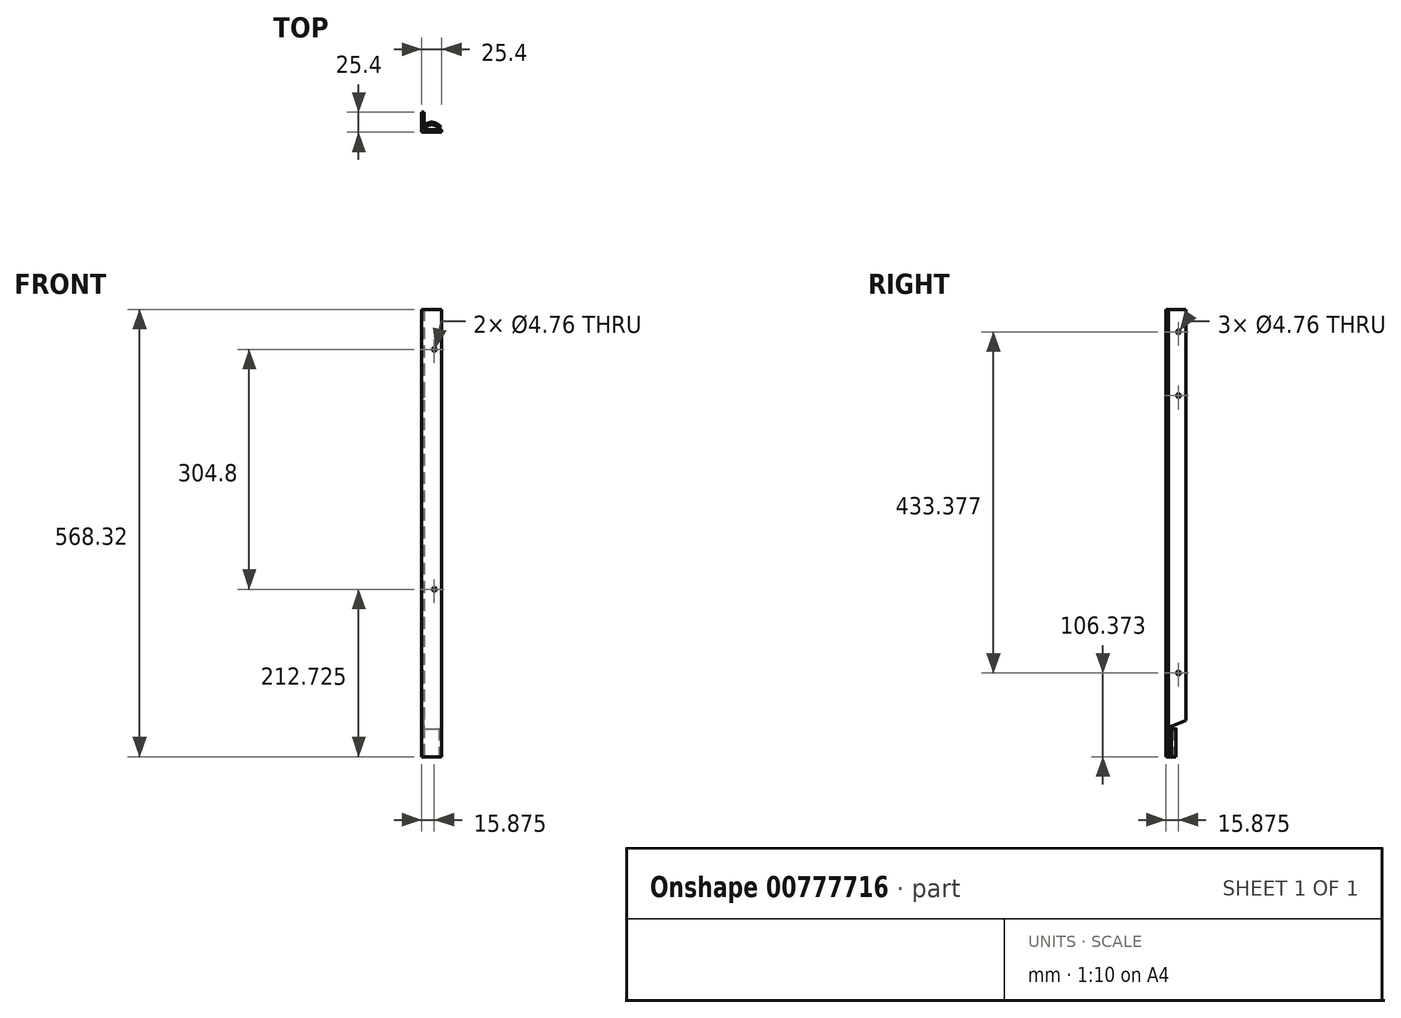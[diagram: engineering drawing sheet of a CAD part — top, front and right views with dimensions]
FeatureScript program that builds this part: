
annotation { "Feature Type Name" : "Feature", "Feature Type Description" : "" }
export const myFeature = defineFeature(function(context is Context, id is Id, definition is map)
    precondition{}
    {
        {
            var Q0;
            Q0=qCreatedBy(makeId("Top.planeOp"),FACE);
            var sketch = newSketch(context, id + "F0", { "sketchPlane" : qUnion([Q0])});
            skLineSegment(sketch, "E0.bottom", {"start": v(0, 0) * mm, "end": v(25.4, 0) * mm});
            skLineSegment(sketch, "E0.top", {"start": v(0, 25.4) * mm, "end": v(3.17, 25.4) * mm});
            skLineSegment(sketch, "E0.left", {"start": v(0, 0) * mm, "end": v(0, 25.4) * mm});
            skLineSegment(sketch, "E0.right", {"start": v(25.4, 0) * mm, "end": v(25.4, 3.18) * mm});
            skLineSegment(sketch, "E1.1", {"start": v(3.17, 3.18) * mm, "end": v(3.17, 25.4) * mm});
            skLineSegment(sketch, "E1.2", {"start": v(3.18, 3.18) * mm, "end": v(25.4, 3.18) * mm});
            skSolve(sketch);
        }
        {
            var Q0;
            Q0 = qSketchRegion(id + "F0", true);
            extrude(context, id + "F1", {"entities" : qUnion([Q0]), "depth" : 568.32 * mm, "offsetDistance" : 25.4 * mm});
        }
        {
            var Q0;
            Q0=makeQuery(id+"F1.opExtrude","SWEPT_FACE",FACE,{"disambiguationData":[OSD([sQuery(id+"F0.wireOp",EDGE,"E0.left")])]});
            var sketch = newSketch(context, id + "F2", { "sketchPlane" : qUnion([Q0])});
            skCircle(sketch, "E2", {"center": v(-15.88, 539.75) * mm, "radius": 2.38 * mm});
            skCircle(sketch, "E3", {"center": v(-15.88, 458.79) * mm, "radius": 2.38 * mm});
            skCircle(sketch, "E4", {"center": v(-15.88, 106.37) * mm, "radius": 2.38 * mm});
            skSolve(sketch);
        }
        {
            var Q0;
            Q0 = qSketchRegion(id + "F2", true);
            extrude(context, id + "F3", {"entities" : qUnion([Q0]), "operationType" : NewBodyOperationType.REMOVE, "oppositeDirection" : true, "depth" : 3.17 * mm, "offsetDistance" : 25.4 * mm});
        }
        {
            var Q0;
            Q0=makeQuery(id+"F1.opExtrude","SWEPT_FACE",FACE,{"disambiguationData":[OSD([sQuery(id+"F0.wireOp",EDGE,"E0.bottom")])]});
            var sketch = newSketch(context, id + "F4", { "sketchPlane" : qUnion([Q0])});
            skCircle(sketch, "E5", {"center": v(15.88, 517.53) * mm, "radius": 2.38 * mm});
            skCircle(sketch, "E6.0.1.0", {"center": v(15.88, 212.73) * mm, "radius": 2.38 * mm});
            skLineSegment(sketch, "E6.direction1", {"start": v(15.88, 517.53) * mm, "end": v(41.28, 517.53) * mm, "construction": true});
            skLineSegment(sketch, "E6.direction2", {"start": v(15.88, 517.53) * mm, "end": v(15.88, 212.73) * mm, "construction": true});
            skSolve(sketch);
        }
        {
            var Q0;
            Q0 = qSketchRegion(id + "F4", true);
            extrude(context, id + "F5", {"entities" : qUnion([Q0]), "operationType" : NewBodyOperationType.REMOVE, "oppositeDirection" : true, "depth" : 3.17 * mm, "offsetDistance" : 25.4 * mm});
        }
        {
            var Q0;
            Q0=makeQuery(id+"F1.opExtrude","SWEPT_FACE",FACE,{"disambiguationData":[OSD([sQuery(id+"F0.wireOp",EDGE,"E0.left")])]});
            var sketch = newSketch(context, id + "F6", { "sketchPlane" : qUnion([Q0])});
            skLineSegment(sketch, "E7", {"start": v(-4.76, 0) * mm, "end": v(-4.76, 38.1) * mm});
            skLineSegment(sketch, "E8", {"start": v(-4.76, 38.1) * mm, "end": v(-25.4, 46.44) * mm});
            skSolve(sketch);
        }
        {
            var Q0;
            Q0 = qSketchRegion(id + "F6", true);
            var Q1;
            {var subQ0=sQuery(id+"F6.wireOp",EDGE,"E7");Q1=makeQuery(id+"F6.imprint","IMPRINT",FACE,{"disambiguationData":[TD([[makeQuery(id+"F6.imprint","IMPRINT",EDGE,{"derivedFrom":subQ0}),1.0]])]});}
            extrude(context, id + "F7", {"entities" : qUnion([Q0, Q1]), "operationType" : NewBodyOperationType.REMOVE, "oppositeDirection" : true, "depth" : 3.17 * mm, "offsetDistance" : 25.4 * mm});
        }
        {
            var Q0;
            Q0=makeQuery(id+"F1.opExtrude","CAP_FACE",FACE,{"disambiguationData":[OSD([sQuery(id+"F0.wireOp",EDGE,"E0.bottom"),sQuery(id+"F0.wireOp",EDGE,"E0.top"),sQuery(id+"F0.wireOp",EDGE,"E0.left"),sQuery(id+"F0.wireOp",EDGE,"E0.right"),sQuery(id+"F0.wireOp",EDGE,"E1.1"),sQuery(id+"F0.wireOp",EDGE,"E1.2")])],"isStart":true});
            var sketch = newSketch(context, id + "F8", { "sketchPlane" : qUnion([Q0])});
            skArc(sketch, "E9", {"start": v(12.36, -9.5) * mm, "mid": v(12.7, -9.53) * mm, "end": v(13.04, -9.5) * mm});
            skArc(sketch, "E10.0", {"start": v(12.01, -12.66) * mm, "mid": v(12.7, -12.7) * mm, "end": v(13.39, -12.66) * mm});
            skArc(sketch, "E11", {"start": v(0, -4.76) * mm, "mid": v(0.2, -5.89) * mm, "end": v(0.8, -6.87) * mm});
            skArc(sketch, "E12", {"start": v(0.8, -6.87) * mm, "mid": v(5.87, -10.81) * mm, "end": v(12.01, -12.66) * mm});
            skArc(sketch, "E13.0", {"start": v(3.17, -4.76) * mm, "mid": v(7.32, -7.99) * mm, "end": v(12.36, -9.5) * mm});
            skLineSegment(sketch, "E14", {"start": v(12.7, -6.35) * mm, "end": v(12.7, -13.47) * mm});
            skArc(sketch, "E15.MirrorCS", {"start": v(24.6, -6.87) * mm, "mid": v(19.53, -10.81) * mm, "end": v(13.39, -12.66) * mm});
            skArc(sketch, "E16.MirrorCS", {"start": v(22.23, -4.76) * mm, "mid": v(18.08, -7.99) * mm, "end": v(13.04, -9.5) * mm});
            skLineSegment(sketch, "E17", {"start": v(24.6, -6.87) * mm, "end": v(22.23, -4.76) * mm});
            skSolve(sketch);
        }
        {
            var Q0;
            Q0 = qSketchRegion(id + "F8", true);
            var Q1;
            Q1=makeQuery(id+"F8.imprint","IMPRINT",FACE,{"disambiguationData":[TD([[makeQuery(id+"F8.imprint","IMPRINT",EDGE,{"derivedFrom":sQuery(id+"F8.wireOp",EDGE,"E11")}),1.0]])]});
            extrude(context, id + "F9", {"entities" : qUnion([Q0, Q1]), "operationType" : NewBodyOperationType.ADD, "oppositeDirection" : true, "depth" : 35.56 * mm, "offsetDistance" : 25.4 * mm});
        }
    });
